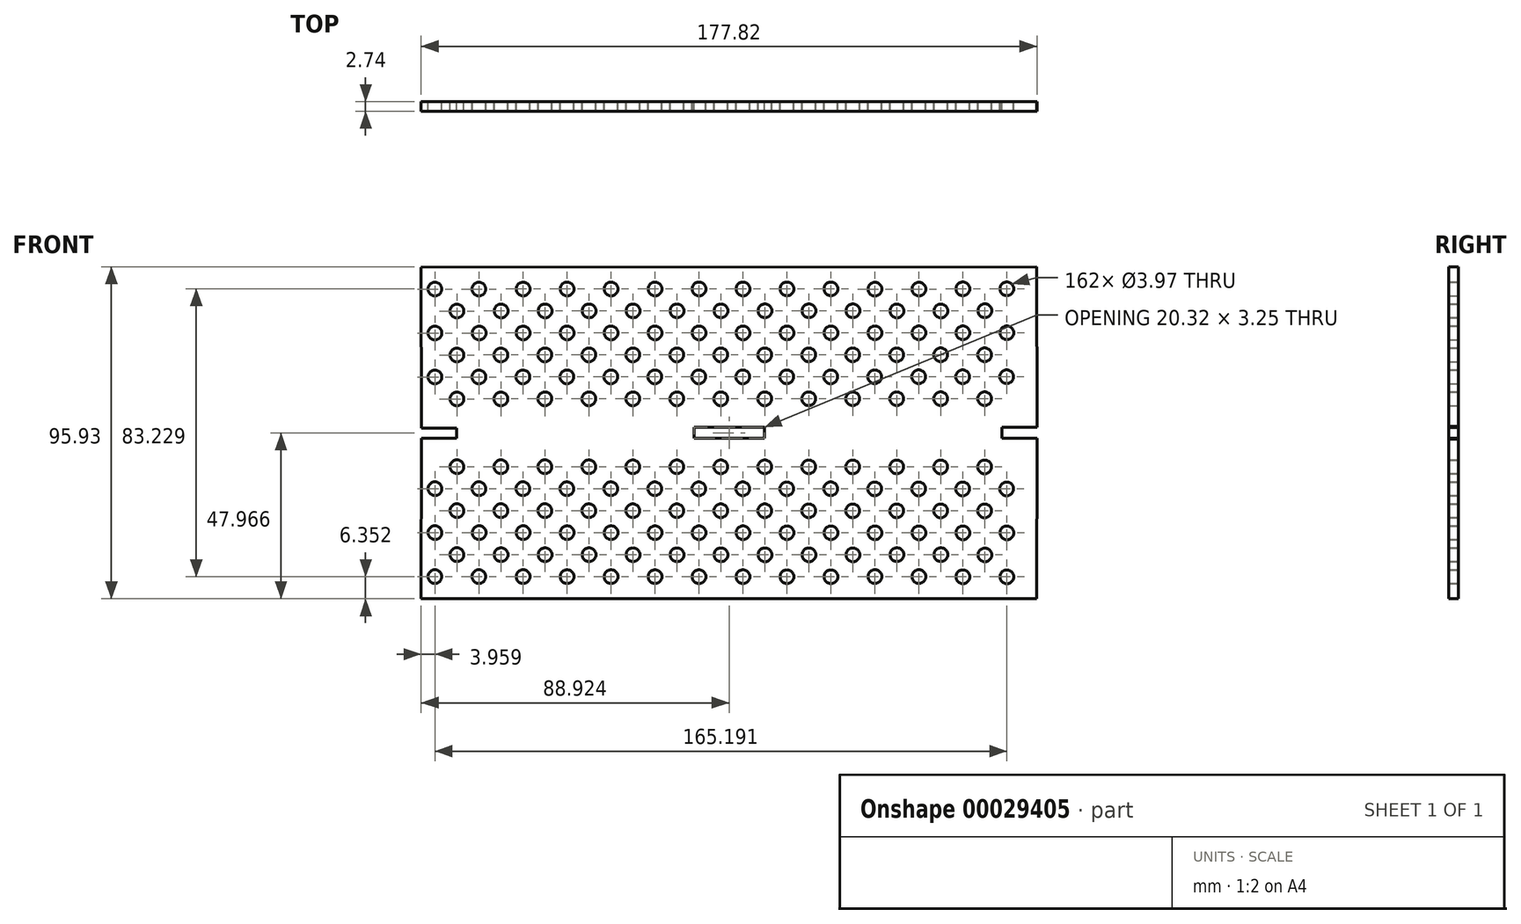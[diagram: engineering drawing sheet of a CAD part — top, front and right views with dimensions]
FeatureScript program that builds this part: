
annotation { "Feature Type Name" : "Feature", "Feature Type Description" : "" }
export const myFeature = defineFeature(function(context is Context, id is Id, definition is map)
    precondition{}
    {
        {
            var Q0;
            Q0=qCreatedBy(makeId("Front.planeOp"),FACE);
            var sketch = newSketch(context, id + "F0", { "sketchPlane" : qUnion([Q0])});
            skCircle(sketch, "E0.MirrorC", {"center": v(-165.92, 41.38) * mm, "radius": 1.98 * mm});
            skCircle(sketch, "E1.MirrorC", {"center": v(-32.5, 73.2) * mm, "radius": 1.98 * mm});
            skCircle(sketch, "E2.MirrorC", {"center": v(-77.02, 41.42) * mm, "radius": 1.98 * mm});
            skCircle(sketch, "E3.MirrorC", {"center": v(-45.27, 47.79) * mm, "radius": 1.98 * mm});
            skCircle(sketch, "E4.MirrorC", {"center": v(-32.49, 60.5) * mm, "radius": 1.98 * mm});
            skLineSegment(sketch, "E5.MirrorCS", {"start": v(-188.94, -16.3) * mm, "end": v(-11.14, -16.38) * mm});
            skCircle(sketch, "E6.MirrorC", {"center": v(-146.8, -9.97) * mm, "radius": 1.98 * mm});
            skCircle(sketch, "E7.MirrorC", {"center": v(-64.32, 21.74) * mm, "radius": 1.98 * mm});
            skCircle(sketch, "E8.MirrorC", {"center": v(-172.28, -9.96) * mm, "radius": 1.98 * mm});
            skCircle(sketch, "E9.MirrorC", {"center": v(-26.22, 9.02) * mm, "radius": 1.98 * mm});
            skCircle(sketch, "E10.MirrorC", {"center": v(-115.04, 66.83) * mm, "radius": 1.98 * mm});
            skCircle(sketch, "E11.MirrorC", {"center": v(-96.07, 47.77) * mm, "radius": 1.98 * mm});
            skCircle(sketch, "E12.MirrorC", {"center": v(-127.82, 54.1) * mm, "radius": 1.98 * mm});
            skCircle(sketch, "E13.MirrorC", {"center": v(-134.17, 15.42) * mm, "radius": 1.98 * mm});
            skCircle(sketch, "E14.MirrorC", {"center": v(-134.1, 73.15) * mm, "radius": 1.98 * mm});
            skCircle(sketch, "E15.MirrorC", {"center": v(-89.64, -3.67) * mm, "radius": 1.98 * mm});
            skCircle(sketch, "E16.MirrorC", {"center": v(-159.5, 73.14) * mm, "radius": 1.98 * mm});
            skCircle(sketch, "E17.MirrorC", {"center": v(-96.07, 15.4) * mm, "radius": 1.98 * mm});
            skCircle(sketch, "E18.MirrorC", {"center": v(-77.02, 9.05) * mm, "radius": 1.98 * mm});
            skCircle(sketch, "E19.MirrorC", {"center": v(-153.22, 54.1) * mm, "radius": 1.98 * mm});
            skCircle(sketch, "E20.MirrorC", {"center": v(-115.12, 54.1) * mm, "radius": 1.98 * mm});
            skCircle(sketch, "E21.MirrorC", {"center": v(-165.92, 9.09) * mm, "radius": 1.98 * mm});
            skCircle(sketch, "E22.MirrorC", {"center": v(-19.87, 15.37) * mm, "radius": 1.98 * mm});
            skCircle(sketch, "E23.MirrorC", {"center": v(-134.17, 47.75) * mm, "radius": 1.98 * mm});
            skCircle(sketch, "E24.MirrorC", {"center": v(-64.24, -3.68) * mm, "radius": 1.98 * mm});
            skCircle(sketch, "E25.MirrorC", {"center": v(-184.97, 15.45) * mm, "radius": 1.98 * mm});
            skCircle(sketch, "E26.MirrorC", {"center": v(-77.02, 21.75) * mm, "radius": 1.98 * mm});
            skCircle(sketch, "E27.MirrorC", {"center": v(-115.12, 9.07) * mm, "radius": 1.98 * mm});
            skCircle(sketch, "E28.MirrorC", {"center": v(-178.62, 21.8) * mm, "radius": 1.98 * mm});
            skCircle(sketch, "E29.MirrorC", {"center": v(-95.99, 60.47) * mm, "radius": 1.98 * mm});
            skCircle(sketch, "E30.MirrorC", {"center": v(-57.9, -9.94) * mm, "radius": 1.98 * mm});
            skCircle(sketch, "E31.MirrorC", {"center": v(-140.44, 66.82) * mm, "radius": 1.98 * mm});
            skCircle(sketch, "E32.MirrorC", {"center": v(-108.77, 47.76) * mm, "radius": 1.98 * mm});
            skCircle(sketch, "E33.MirrorC", {"center": v(-184.98, 73.13) * mm, "radius": 1.98 * mm});
            skCircle(sketch, "E34.MirrorC", {"center": v(-140.44, -3.65) * mm, "radius": 1.98 * mm});
            skCircle(sketch, "E35.MirrorC", {"center": v(-115.04, -3.66) * mm, "radius": 1.98 * mm});
            skCircle(sketch, "E36.MirrorC", {"center": v(-108.69, 2.71) * mm, "radius": 1.98 * mm});
            skCircle(sketch, "E37.MirrorC", {"center": v(-153.22, 41.4) * mm, "radius": 1.98 * mm});
            skCircle(sketch, "E38.MirrorC", {"center": v(-96, -10) * mm, "radius": 1.98 * mm});
            skCircle(sketch, "E39.MirrorC", {"center": v(-159.49, 60.44) * mm, "radius": 1.98 * mm});
            skCircle(sketch, "E40.MirrorC", {"center": v(-153.14, -3.64) * mm, "radius": 1.98 * mm});
            skCircle(sketch, "E41.MirrorC", {"center": v(-172.19, 2.74) * mm, "radius": 1.98 * mm});
            skCircle(sketch, "E42.MirrorC", {"center": v(-95.99, 2.7) * mm, "radius": 1.98 * mm});
            skCircle(sketch, "E43.MirrorC", {"center": v(-127.82, 9.07) * mm, "radius": 1.98 * mm});
            skCircle(sketch, "E44.MirrorC", {"center": v(-45.2, -9.95) * mm, "radius": 1.98 * mm});
            skCircle(sketch, "E45.MirrorC", {"center": v(-159.5, -9.96) * mm, "radius": 1.98 * mm});
            skCircle(sketch, "E46.MirrorC", {"center": v(-57.9, 73.12) * mm, "radius": 1.98 * mm});
            skCircle(sketch, "E47.MirrorC", {"center": v(-102.42, 41.41) * mm, "radius": 1.98 * mm});
            skCircle(sketch, "E48.MirrorC", {"center": v(-102.34, -3.66) * mm, "radius": 1.98 * mm});
            skCircle(sketch, "E49.MirrorC", {"center": v(-45.19, 60.49) * mm, "radius": 1.98 * mm});
            skCircle(sketch, "E50.MirrorC", {"center": v(-64.32, 9.04) * mm, "radius": 1.98 * mm});
            skCircle(sketch, "E51.MirrorC", {"center": v(-32.57, 15.38) * mm, "radius": 1.98 * mm});
            skCircle(sketch, "E52.MirrorC", {"center": v(-51.54, -3.62) * mm, "radius": 1.98 * mm});
            skCircle(sketch, "E53.MirrorC", {"center": v(-89.72, 54.12) * mm, "radius": 1.98 * mm});
            skCircle(sketch, "E54.MirrorC", {"center": v(-32.57, 47.8) * mm, "radius": 1.98 * mm});
            skCircle(sketch, "E55.MirrorC", {"center": v(-76.94, 66.85) * mm, "radius": 1.98 * mm});
            skCircle(sketch, "E56.MirrorC", {"center": v(-19.87, 47.8) * mm, "radius": 1.98 * mm});
            skCircle(sketch, "E57.MirrorC", {"center": v(-70.67, 47.75) * mm, "radius": 1.98 * mm});
            skCircle(sketch, "E58.MirrorC", {"center": v(-38.92, 41.44) * mm, "radius": 1.98 * mm});
            skCircle(sketch, "E59.MirrorC", {"center": v(-134.09, 2.72) * mm, "radius": 1.98 * mm});
            skCircle(sketch, "E60.MirrorC", {"center": v(-19.8, 73.2) * mm, "radius": 1.98 * mm});
            skCircle(sketch, "E61.MirrorC", {"center": v(-57.97, 47.78) * mm, "radius": 1.98 * mm});
            skCircle(sketch, "E62.MirrorC", {"center": v(-83.3, -10) * mm, "radius": 1.98 * mm});
            skCircle(sketch, "E63.MirrorC", {"center": v(-184.97, 47.73) * mm, "radius": 1.98 * mm});
            skCircle(sketch, "E64.MirrorC", {"center": v(-51.62, 9.04) * mm, "radius": 1.98 * mm});
            skCircle(sketch, "E65.MirrorC", {"center": v(-108.69, 60.46) * mm, "radius": 1.98 * mm});
            skCircle(sketch, "E66.MirrorC", {"center": v(-115.12, 21.77) * mm, "radius": 1.98 * mm});
            skCircle(sketch, "E67.MirrorC", {"center": v(-140.52, 41.4) * mm, "radius": 1.98 * mm});
            skCircle(sketch, "E68.MirrorC", {"center": v(-159.57, 47.74) * mm, "radius": 1.98 * mm});
            skCircle(sketch, "E69.MirrorC", {"center": v(-121.39, 60.45) * mm, "radius": 1.98 * mm});
            skCircle(sketch, "E70.MirrorC", {"center": v(-127.82, 21.77) * mm, "radius": 1.98 * mm});
            skLineSegment(sketch, "E71.MirrorCS", {"start": v(-110.18, 30.26) * mm, "end": v(-110.17, 30.26) * mm});
            skCircle(sketch, "E72.MirrorC", {"center": v(-32.5, -10.02) * mm, "radius": 1.98 * mm});
            skCircle(sketch, "E73.MirrorC", {"center": v(-159.57, 15.44) * mm, "radius": 1.98 * mm});
            skCircle(sketch, "E74.MirrorC", {"center": v(-45.27, 15.38) * mm, "radius": 1.98 * mm});
            skCircle(sketch, "E75.MirrorC", {"center": v(-38.92, 9.03) * mm, "radius": 1.98 * mm});
            skCircle(sketch, "E76.MirrorC", {"center": v(-57.97, 15.39) * mm, "radius": 1.98 * mm});
            skCircle(sketch, "E77.MirrorC", {"center": v(-178.63, -3.6) * mm, "radius": 1.98 * mm});
            skCircle(sketch, "E78.MirrorC", {"center": v(-57.89, 60.48) * mm, "radius": 1.98 * mm});
            skCircle(sketch, "E79.MirrorC", {"center": v(-38.84, 66.8) * mm, "radius": 1.98 * mm});
            skCircle(sketch, "E80.MirrorC", {"center": v(-83.37, 47.77) * mm, "radius": 1.98 * mm});
            skCircle(sketch, "E81.MirrorC", {"center": v(-70.59, 60.48) * mm, "radius": 1.98 * mm});
            skCircle(sketch, "E82.MirrorC", {"center": v(-70.6, 73.18) * mm, "radius": 1.98 * mm});
            skCircle(sketch, "E83.MirrorC", {"center": v(-165.84, -3.64) * mm, "radius": 1.98 * mm});
            skCircle(sketch, "E84.MirrorC", {"center": v(-178.62, 9.1) * mm, "radius": 1.98 * mm});
            skCircle(sketch, "E85.MirrorC", {"center": v(-146.87, 15.43) * mm, "radius": 1.98 * mm});
            skCircle(sketch, "E86.MirrorC", {"center": v(-108.7, -9.99) * mm, "radius": 1.98 * mm});
            skCircle(sketch, "E87.MirrorC", {"center": v(-159.49, 2.74) * mm, "radius": 1.98 * mm});
            skCircle(sketch, "E88.MirrorC", {"center": v(-26.14, -3.7) * mm, "radius": 1.98 * mm});
            skLineSegment(sketch, "E89.MirrorCS", {"start": v(-188.94, 79.47) * mm, "end": v(-11.14, 79.55) * mm});
            skCircle(sketch, "E90.MirrorC", {"center": v(-172.27, 47.73) * mm, "radius": 1.98 * mm});
            skCircle(sketch, "E91.MirrorC", {"center": v(-146.8, 73.14) * mm, "radius": 1.98 * mm});
            skCircle(sketch, "E92.MirrorC", {"center": v(-178.63, 66.78) * mm, "radius": 1.98 * mm});
            skCircle(sketch, "E93.MirrorC", {"center": v(-102.34, 66.84) * mm, "radius": 1.98 * mm});
            skCircle(sketch, "E94.MirrorC", {"center": v(-140.52, 21.78) * mm, "radius": 1.98 * mm});
            skCircle(sketch, "E95.MirrorC", {"center": v(-38.84, -3.63) * mm, "radius": 1.98 * mm});
            skCircle(sketch, "E96.MirrorC", {"center": v(-153.22, 9.08) * mm, "radius": 1.98 * mm});
            skCircle(sketch, "E97.MirrorC", {"center": v(-184.98, -9.95) * mm, "radius": 1.98 * mm});
            skCircle(sketch, "E98.MirrorC", {"center": v(-108.77, 15.41) * mm, "radius": 1.98 * mm});
            skCircle(sketch, "E99.MirrorC", {"center": v(-102.42, 54.11) * mm, "radius": 1.98 * mm});
            skCircle(sketch, "E100.MirrorC", {"center": v(-108.7, 73.16) * mm, "radius": 1.98 * mm});
            skCircle(sketch, "E101.MirrorC", {"center": v(-89.72, 41.42) * mm, "radius": 1.98 * mm});
            skCircle(sketch, "E102.MirrorC", {"center": v(-172.19, 60.43) * mm, "radius": 1.98 * mm});
            skCircle(sketch, "E103.MirrorC", {"center": v(-89.64, 66.84) * mm, "radius": 1.98 * mm});
            skCircle(sketch, "E104.MirrorC", {"center": v(-165.84, 66.8) * mm, "radius": 1.98 * mm});
            skCircle(sketch, "E105.MirrorC", {"center": v(-32.49, 2.68) * mm, "radius": 1.98 * mm});
            skCircle(sketch, "E106.MirrorC", {"center": v(-89.72, 9.05) * mm, "radius": 1.98 * mm});
            skCircle(sketch, "E107.MirrorC", {"center": v(-134.1, -9.98) * mm, "radius": 1.98 * mm});
            skCircle(sketch, "E108.MirrorC", {"center": v(-146.79, 2.73) * mm, "radius": 1.98 * mm});
            skCircle(sketch, "E109.MirrorC", {"center": v(-153.14, 66.81) * mm, "radius": 1.98 * mm});
            skCircle(sketch, "E110.MirrorC", {"center": v(-83.3, 73.17) * mm, "radius": 1.98 * mm});
            skCircle(sketch, "E111.MirrorC", {"center": v(-51.62, 41.44) * mm, "radius": 1.98 * mm});
            skCircle(sketch, "E112.MirrorC", {"center": v(-45.19, 2.68) * mm, "radius": 1.98 * mm});
            skCircle(sketch, "E113.MirrorC", {"center": v(-26.22, 41.45) * mm, "radius": 1.98 * mm});
            skCircle(sketch, "E114.MirrorC", {"center": v(-178.62, 41.38) * mm, "radius": 1.98 * mm});
            skCircle(sketch, "E115.MirrorC", {"center": v(-64.24, 66.85) * mm, "radius": 1.98 * mm});
            skCircle(sketch, "E116.MirrorC", {"center": v(-19.79, 60.5) * mm, "radius": 1.98 * mm});
            skCircle(sketch, "E117.MirrorC", {"center": v(-172.28, 73.13) * mm, "radius": 1.98 * mm});
            skCircle(sketch, "E118.MirrorC", {"center": v(-127.82, 41.4) * mm, "radius": 1.98 * mm});
            skCircle(sketch, "E119.MirrorC", {"center": v(-96, 73.17) * mm, "radius": 1.98 * mm});
            skCircle(sketch, "E120.MirrorC", {"center": v(-51.62, 54.14) * mm, "radius": 1.98 * mm});
            skCircle(sketch, "E121.MirrorC", {"center": v(-172.27, 15.44) * mm, "radius": 1.98 * mm});
            skCircle(sketch, "E122.MirrorC", {"center": v(-102.42, 9.06) * mm, "radius": 1.98 * mm});
            skCircle(sketch, "E123.MirrorC", {"center": v(-76.94, -3.68) * mm, "radius": 1.98 * mm});
            skCircle(sketch, "E124.MirrorC", {"center": v(-83.29, 2.7) * mm, "radius": 1.98 * mm});
            skCircle(sketch, "E125.MirrorC", {"center": v(-121.47, 15.42) * mm, "radius": 1.98 * mm});
            skLineSegment(sketch, "E126.MirrorCS", {"start": v(-11.14, -16.38) * mm, "end": v(-11.12, 29.73) * mm});
            skCircle(sketch, "E127.MirrorC", {"center": v(-140.52, 9.08) * mm, "radius": 1.98 * mm});
            skCircle(sketch, "E128.MirrorC", {"center": v(-146.79, 60.44) * mm, "radius": 1.98 * mm});
            skCircle(sketch, "E129.MirrorC", {"center": v(-121.47, 47.75) * mm, "radius": 1.98 * mm});
            skCircle(sketch, "E130.MirrorC", {"center": v(-115.12, 41.4) * mm, "radius": 1.98 * mm});
            skLineSegment(sketch, "E131.MirrorCS", {"start": v(-11.14, 79.55) * mm, "end": v(-11.12, 33.48) * mm});
            skCircle(sketch, "E132.MirrorC", {"center": v(-38.92, 21.73) * mm, "radius": 1.98 * mm});
            skCircle(sketch, "E133.MirrorC", {"center": v(-184.98, 60.43) * mm, "radius": 1.98 * mm});
            skCircle(sketch, "E134.MirrorC", {"center": v(-51.54, 66.8) * mm, "radius": 1.98 * mm});
            skCircle(sketch, "E135.MirrorC", {"center": v(-38.92, 54.14) * mm, "radius": 1.98 * mm});
            skCircle(sketch, "E136.MirrorC", {"center": v(-127.74, -3.65) * mm, "radius": 1.98 * mm});
            skCircle(sketch, "E137.MirrorC", {"center": v(-153.22, 21.78) * mm, "radius": 1.98 * mm});
            skCircle(sketch, "E138.MirrorC", {"center": v(-102.42, 21.76) * mm, "radius": 1.98 * mm});
            skCircle(sketch, "E139.MirrorC", {"center": v(-83.37, 15.4) * mm, "radius": 1.98 * mm});
            skCircle(sketch, "E140.MirrorC", {"center": v(-57.89, 2.69) * mm, "radius": 1.98 * mm});
            skCircle(sketch, "E141.MirrorC", {"center": v(-45.2, 73.12) * mm, "radius": 1.98 * mm});
            skCircle(sketch, "E142.MirrorC", {"center": v(-64.32, 54.13) * mm, "radius": 1.98 * mm});
            skCircle(sketch, "E143.MirrorC", {"center": v(-121.4, 73.15) * mm, "radius": 1.98 * mm});
            skCircle(sketch, "E144.MirrorC", {"center": v(-70.67, 15.42) * mm, "radius": 1.98 * mm});
            skCircle(sketch, "E145.MirrorC", {"center": v(-19.8, -10.03) * mm, "radius": 1.98 * mm});
            skCircle(sketch, "E146.MirrorC", {"center": v(-70.59, 2.7) * mm, "radius": 1.98 * mm});
            skCircle(sketch, "E147.MirrorC", {"center": v(-140.52, 54.1) * mm, "radius": 1.98 * mm});
            skCircle(sketch, "E148.MirrorC", {"center": v(-26.14, 66.87) * mm, "radius": 1.98 * mm});
            skCircle(sketch, "E149.MirrorC", {"center": v(-64.32, 41.43) * mm, "radius": 1.98 * mm});
            skCircle(sketch, "E150.MirrorC", {"center": v(-134.09, 60.45) * mm, "radius": 1.98 * mm});
            skCircle(sketch, "E151.MirrorC", {"center": v(-83.29, 60.47) * mm, "radius": 1.98 * mm});
            skCircle(sketch, "E152.MirrorC", {"center": v(-51.62, 21.74) * mm, "radius": 1.98 * mm});
            skCircle(sketch, "E153.MirrorC", {"center": v(-121.39, 2.72) * mm, "radius": 1.98 * mm});
            skCircle(sketch, "E154.MirrorC", {"center": v(-70.6, -10) * mm, "radius": 1.98 * mm});
            skCircle(sketch, "E155.MirrorC", {"center": v(-184.98, 2.75) * mm, "radius": 1.98 * mm});
            skCircle(sketch, "E156.MirrorC", {"center": v(-165.92, 21.79) * mm, "radius": 1.98 * mm});
            skCircle(sketch, "E157.MirrorC", {"center": v(-146.87, 47.74) * mm, "radius": 1.98 * mm});
            skCircle(sketch, "E158.MirrorC", {"center": v(-127.74, 66.83) * mm, "radius": 1.98 * mm});
            skCircle(sketch, "E159.MirrorC", {"center": v(-26.22, 21.72) * mm, "radius": 1.98 * mm});
            skCircle(sketch, "E160.MirrorC", {"center": v(-77.02, 54.12) * mm, "radius": 1.98 * mm});
            skCircle(sketch, "E161.MirrorC", {"center": v(-178.62, 54.08) * mm, "radius": 1.98 * mm});
            skCircle(sketch, "E162.MirrorC", {"center": v(-165.92, 54.08) * mm, "radius": 1.98 * mm});
            skCircle(sketch, "E163.MirrorC", {"center": v(-26.22, 54.15) * mm, "radius": 1.98 * mm});
            skCircle(sketch, "E164.MirrorC", {"center": v(-121.4, -9.98) * mm, "radius": 1.98 * mm});
            skCircle(sketch, "E165.MirrorC", {"center": v(-89.72, 21.75) * mm, "radius": 1.98 * mm});
            skCircle(sketch, "E166.MirrorC", {"center": v(-19.79, 2.67) * mm, "radius": 1.98 * mm});
            skLineSegment(sketch, "E167", {"start": v(-178.76, 30.12) * mm, "end": v(-178.76, 32.87) * mm});
            skLineSegment(sketch, "E168", {"start": v(-21.28, 30.23) * mm, "end": v(-21.28, 32.97) * mm});
            skLineSegment(sketch, "E169", {"start": v(-11.12, 35.51) * mm, "end": v(-11.12, 35.51) * mm});
            skLineSegment(sketch, "E170", {"start": v(-11.12, 27.3) * mm, "end": v(-11.12, 27.3) * mm});
            skLineSegment(sketch, "E171", {"start": v(-21.28, 30.23) * mm, "end": v(-21.28, 29.98) * mm});
            skLineSegment(sketch, "E172", {"start": v(-21.28, 32.97) * mm, "end": v(-21.28, 33.22) * mm});
            skLineSegment(sketch, "E173", {"start": v(-11.12, 33.48) * mm, "end": v(-11.12, 33.48) * mm});
            skLineSegment(sketch, "E174", {"start": v(-11.12, 29.73) * mm, "end": v(-11.12, 29.73) * mm});
            skLineSegment(sketch, "E175", {"start": v(-110.17, 30.26) * mm, "end": v(-110.17, 30) * mm});
            skLineSegment(sketch, "E176", {"start": v(-110.18, 32.91) * mm, "end": v(-110.17, 30.26) * mm});
            skLineSegment(sketch, "E177", {"start": v(-89.85, 32.96) * mm, "end": v(-89.85, 30.21) * mm});
            skLineSegment(sketch, "E178", {"start": v(-110.18, 32.91) * mm, "end": v(-110.18, 33.16) * mm});
            skLineSegment(sketch, "E179", {"start": v(-89.85, 29.96) * mm, "end": v(-89.85, 30.21) * mm});
            skLineSegment(sketch, "E180", {"start": v(-89.85, 33.21) * mm, "end": v(-89.85, 32.96) * mm});
            skLineSegment(sketch, "E181", {"start": v(-178.76, 32.87) * mm, "end": v(-178.76, 33.12) * mm});
            skLineSegment(sketch, "E182", {"start": v(-178.76, 30.12) * mm, "end": v(-178.76, 29.86) * mm});
            skLineSegment(sketch, "E183", {"start": v(-188.92, 33.37) * mm, "end": v(-188.94, 79.47) * mm});
            skLineSegment(sketch, "E184", {"start": v(-188.92, 29.61) * mm, "end": v(-188.94, -16.3) * mm});
            skLineSegment(sketch, "E185", {"start": v(-188.92, 33.12) * mm, "end": v(-188.92, 33.37) * mm});
            skLineSegment(sketch, "E186", {"start": v(-188.92, 29.87) * mm, "end": v(-188.92, 29.61) * mm});
            skPoint(sketch, "E187.orphan", {"position": v(-178.76, 29.6) * mm});
            skPoint(sketch, "E188.orphan", {"position": v(-178.76, 33.38) * mm});
            skLineSegment(sketch, "E189", {"start": v(-110.18, 33.16) * mm, "end": v(-89.85, 33.21) * mm});
            skPoint(sketch, "E189.startSnap0", {"position": v(-110.18, 33.16) * mm});
            skLineSegment(sketch, "E190", {"start": v(-110.17, 30) * mm, "end": v(-89.85, 29.96) * mm});
            skPoint(sketch, "E191.orphan", {"position": v(-110.17, 29.75) * mm});
            skPoint(sketch, "E192.orphan", {"position": v(-110.18, 33.42) * mm});
            skPoint(sketch, "E193.orphan", {"position": v(-89.85, 29.7) * mm});
            skPoint(sketch, "E194.orphan", {"position": v(-89.85, 33.47) * mm});
            skLineSegment(sketch, "E195", {"start": v(-178.76, 30) * mm, "end": v(-188.92, 30) * mm});
            skLineSegment(sketch, "E196", {"start": v(-188.92, 30) * mm, "end": v(-188.92, 29.87) * mm});
            skLineSegment(sketch, "E197", {"start": v(-178.76, 33) * mm, "end": v(-188.92, 33) * mm});
            skLineSegment(sketch, "E198", {"start": v(-188.92, 33) * mm, "end": v(-188.92, 33.12) * mm});
            skLineSegment(sketch, "E199", {"start": v(-21.28, 29.98) * mm, "end": v(-11.12, 29.98) * mm});
            skLineSegment(sketch, "E200", {"start": v(-11.12, 29.98) * mm, "end": v(-11.12, 29.73) * mm});
            skLineSegment(sketch, "E201", {"start": v(-21.28, 33.22) * mm, "end": v(-11.12, 33.22) * mm});
            skLineSegment(sketch, "E202", {"start": v(-11.12, 33.22) * mm, "end": v(-11.12, 33.48) * mm});
            skPoint(sketch, "E203.orphan", {"position": v(-21.28, 29.72) * mm});
            skPoint(sketch, "E204.orphan", {"position": v(-21.28, 33.47) * mm});
            skSolve(sketch);
        }
        {
            var Q0;
            Q0=makeQuery(id+"F0.imprint","IMPRINT",FACE,{"disambiguationData":[TD([[makeQuery(id+"F0.imprint","IMPRINT",EDGE,{"derivedFrom":sQuery(id+"F0.wireOp",EDGE,"E0.MirrorC")}),-1.0]])]});
            extrude(context, id + "F1", {"entities" : qUnion([Q0]), "depth" : 2.74 * mm});
        }
    });
